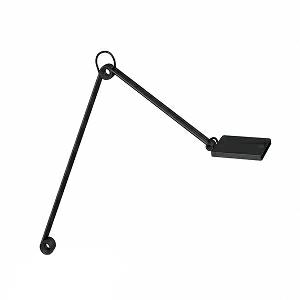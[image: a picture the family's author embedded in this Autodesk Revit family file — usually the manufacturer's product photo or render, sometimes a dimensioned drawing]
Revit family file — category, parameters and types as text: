
# Revit family: para_mi_-_ftl_108_r__930_00644079_d4ea
name_source: partatom
category: Lighting Fixtures
units: mm (PartAtom-declared; Revit-internal decimal feet)

## family parameters
Cut with Voids When Loaded = No
Host = Face
Light Source = No
Part Type = Normal
Room Calculation Point = No
Round Connector Dimension = Use Diameter
Shared = No

## types (1)
- PARA.MI - FTL 108 R /930 (1 x LED, 580 lm, 3000K)
    Apparent Load = 7 VA
    Approval mark = CE
    CIE Flux Codes = 70 94 99 100 100
    Color Rendering = 90-100
    Color Temperature = 3000K
    Control Gear = Electronic ballast
    Default Elevation = 1800 mm
    Description = FTL 108 R|Task luminaire|light source: LED|work equipment: Electronic plug-in transformer|connected load: 100-240 V, 50/60 Hz|Power consumption: approx. 7 W|luminous flux: 580 lm|luminous efficacy: 82 lm/W|Illuminance efficiency factor: 107 lx/W|colour temperature: Warm white, ca. 3000 K|color rendering index (CRI): >= 90|chromaticity tolerance:  3 SDCM|class of protection: II with plug-in power supply, III without plug-in power supply|technology: Continuously dimmable|luminaire body|material: Aluminium|surface: Painted|colour: Black|lamp cover: Plastic, Clear|tubular sections|material: Tubular aluminium section|surface: Painted|colour: Jet black|weight (net): approx. 1.0 kg|mains lead: 3.00 m Mains plug BS 1363, CEE 7/XVI, NEMA 1-15P|Fastening: Adaptor (accessory), Table base (accessory), Table clamp (accessory), Tap16|glare control: Reflector|special features: Automatic switchoff adjustable, Push button in luminaire head, Behaviour at net recovery adjustable|Approval mark: C - ETL - US (F. CAN U. USA), VDE - ENEC SEP LIGHT & POWER SUPPLY UNIT|
    Height = 12 mm  [stored 0.0393701 ft]
    Lamp = 1 x LED
    Lamp Light Flux = 580 lm
    Lamp count = 1
    Length = 123 mm
    Luminous efficacy = 83 lm/W
    Manufacturer = Waldmann
    ModVariant = No
    Model = 00644079
    Mounting Place = Table
    Mounting Type = Surface mounted
    Number of Poles = 1
    OnlyDefault = Yes
    Power Factor = 1
    Product Name = PARA.MI - FTL 108 R /930
    Product group = Task luminaire (office)
    ProductGroupID = 21
    Protection Class = Protection class II
    Protection Degree = IP 40
    RLX_Detail_Level = 1
    RLX_Emergency_Light_Flux = 0 lm
    RLX_Emergency_Type = 0
    RLX_Emergency_Type_DB = No
    RlxData = <blob elided: 96557 chars, md5=676c867e>
    Socket = socket
    Standby Power = 0 W
    System Light Flux = 580 lm
    System Power = 7 W
    Type Comments = Product without accessories
    Type Image = 113148000-00644091.jpg
    URL = http://relux.com
    VarID = ---
    Voltage = 230 V
    Voltage Range = 220-240 V
    Weight = 0.00 kg
    Width = 0 mm  [stored 0 ft]

note: [stored X ft] marks values corroborated as IEEE doubles in the binary element streams (Revit-internal decimal feet)

## geometry (parser evidence)
native form markers: Blend x4, Sweep x14
no freeform markers — native parametric forms only
